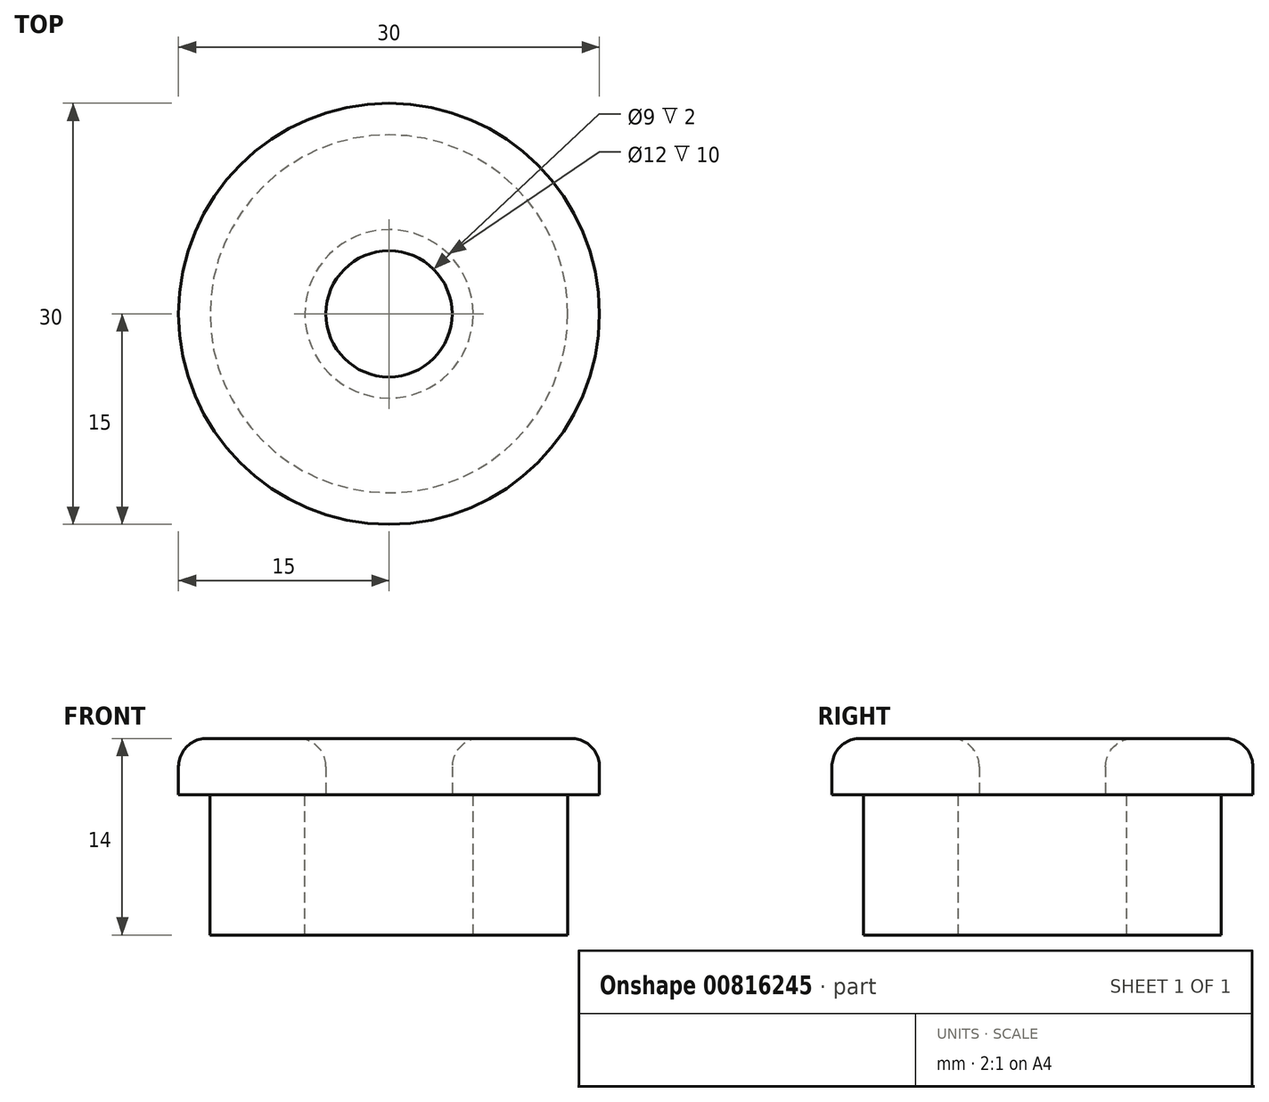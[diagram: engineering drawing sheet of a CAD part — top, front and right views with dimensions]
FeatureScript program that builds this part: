
annotation { "Feature Type Name" : "Feature", "Feature Type Description" : "" }
export const myFeature = defineFeature(function(context is Context, id is Id, definition is map)
    precondition{}
    {
        {
            var Q0;
            Q0=qCreatedBy(makeId("Top.planeOp"),FACE);
            var sketch = newSketch(context, id + "F0", { "sketchPlane" : qUnion([Q0])});
            skCircle(sketch, "E0", {"center": v(0, 0) * mm, "radius": 15 * mm});
            skCircle(sketch, "E1", {"center": v(0, 0) * mm, "radius": 4.5 * mm});
            skSolve(sketch);
        }
        {
            var Q0;
            Q0=makeQuery(id+"F0.imprint","IMPRINT",FACE,{"disambiguationData":[TD([[makeQuery(id+"F0.imprint","IMPRINT",EDGE,{"derivedFrom":sQuery(id+"F0.wireOp",EDGE,"E0")}),1.0]])]});
            extrude(context, id + "F1", {"entities" : qUnion([Q0]), "depth" : 4 * mm, "offsetDistance" : 25 * mm});
        }
        {
            var Q0;
            Q0=makeQuery(id+"F1.opExtrude","CAP_FACE",FACE,{"disambiguationData":[OSD([sQuery(id+"F0.wireOp",EDGE,"E0"),sQuery(id+"F0.wireOp",EDGE,"E1")])],"isStart":true});
            var sketch = newSketch(context, id + "F2", { "sketchPlane" : qUnion([Q0])});
            skCircle(sketch, "E2", {"center": v(0, 0) * mm, "radius": 12.75 * mm});
            skCircle(sketch, "E3", {"center": v(0, 0) * mm, "radius": 6 * mm});
            skSolve(sketch);
        }
        {
            var Q0;
            Q0=makeQuery(id+"F2.imprint","IMPRINT",FACE,{"disambiguationData":[TD([[makeQuery(id+"F2.imprint","IMPRINT",EDGE,{"derivedFrom":sQuery(id+"F2.wireOp",EDGE,"E2")}),1.0]])]});
            extrude(context, id + "F3", {"entities" : qUnion([Q0]), "operationType" : NewBodyOperationType.ADD, "depth" : 10 * mm, "offsetDistance" : 25 * mm});
        }
        {
            var Q0;
            Q0=makeQuery(id+"F1.opExtrude","CAP_FACE",FACE,{"disambiguationData":[OSD([sQuery(id+"F0.wireOp",EDGE,"E0"),sQuery(id+"F0.wireOp",EDGE,"E1")])],"isStart":false});
            fillet(context, id + "F4", {"entities" : qUnion([Q0]), "radius" : 2 * mm, "tangentPropagation" : true, "allowEdgeOverflow" : false});
        }
    });
